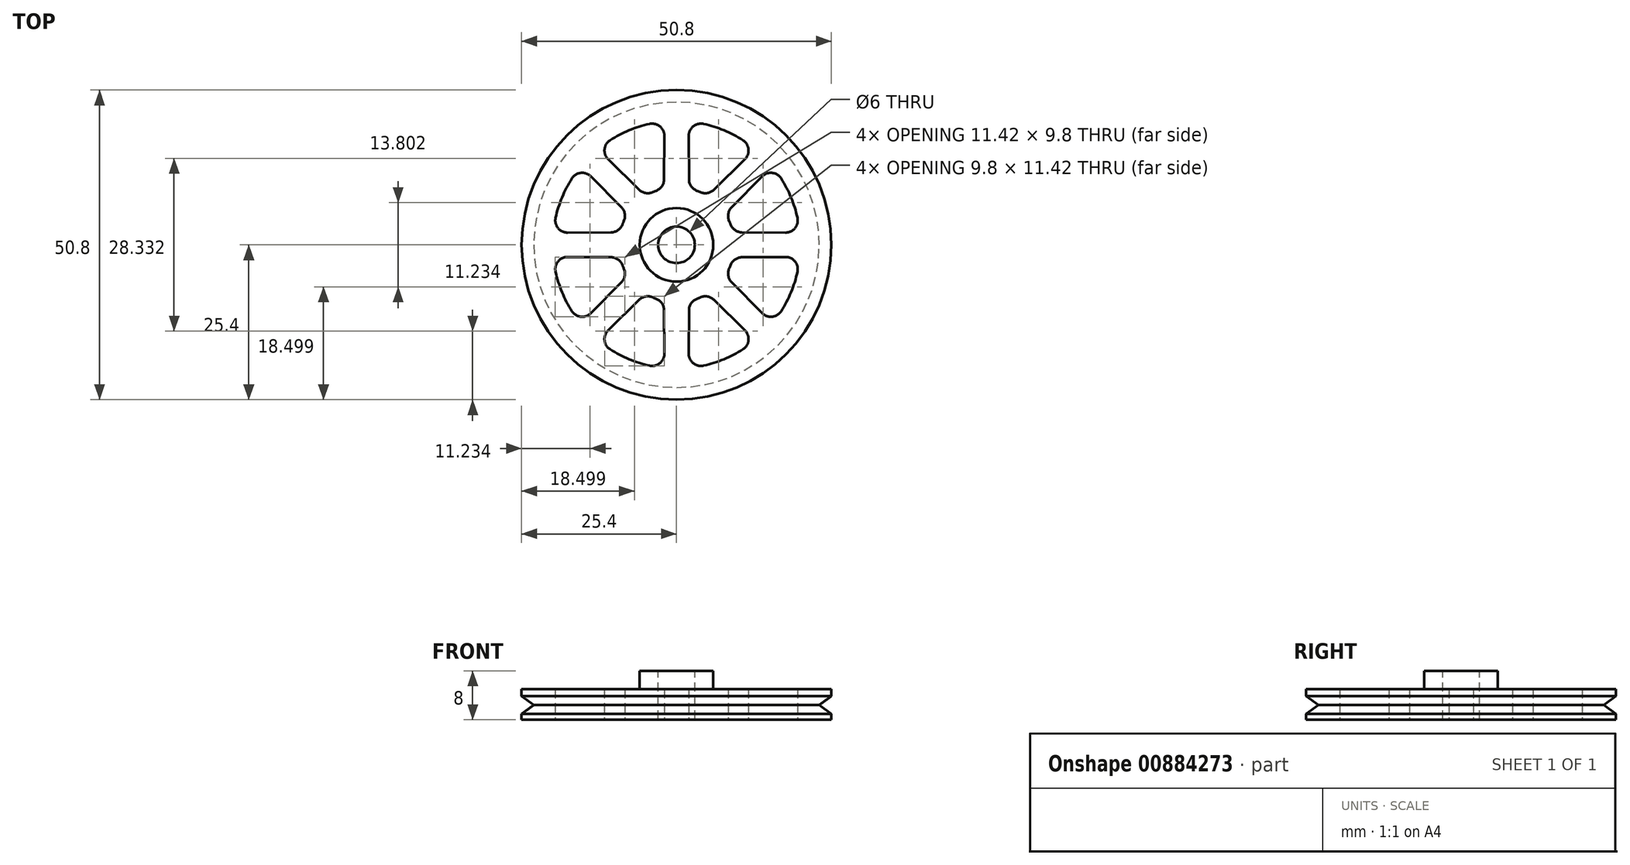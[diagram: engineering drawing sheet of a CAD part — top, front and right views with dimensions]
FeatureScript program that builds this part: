
annotation { "Feature Type Name" : "Feature", "Feature Type Description" : "" }
export const myFeature = defineFeature(function(context is Context, id is Id, definition is map)
    precondition{}
    {
        {
            var Q0;
            Q0=qCreatedBy(makeId("Top.planeOp"),FACE);
            var sketch = newSketch(context, id + "F0", { "sketchPlane" : qUnion([Q0])});
            skCircle(sketch, "E0", {"center": v(0, 0) * mm, "radius": 25.4 * mm});
            skCircle(sketch, "E1", {"center": v(0, 0) * mm, "radius": 3.12 * mm});
            skArc(sketch, "E2.0", {"start": v(-4.44, 19.83) * mm, "mid": v(-7.78, 18.77) * mm, "end": v(-10.88, 17.16) * mm});
            skArc(sketch, "E3.0", {"start": v(-3.34, 8.87) * mm, "mid": v(-3.63, 8.75) * mm, "end": v(-3.9, 8.63) * mm});
            skLineSegment(sketch, "E4.0", {"start": v(-2, 17.87) * mm, "end": v(-2.04, 10.73) * mm});
            skLineSegment(sketch, "E5.0", {"start": v(2, 17.87) * mm, "end": v(2.04, 10.73) * mm});
            skPoint(sketch, "E6.orphan", {"position": v(0, 22.85) * mm});
            skPoint(sketch, "E7.visualSharp", {"position": v(-1.99, 20.22) * mm});
            skArc(sketch, "E7.filletArc", {"start": v(-2, 17.87) * mm, "mid": v(-2.74, 19.44) * mm, "end": v(-4.44, 19.83) * mm});
            skPoint(sketch, "E8.visualSharp", {"position": v(1.99, 20.22) * mm});
            skArc(sketch, "E8.filletArc", {"start": v(4.44, 19.83) * mm, "mid": v(2.74, 19.44) * mm, "end": v(2, 17.87) * mm});
            skPoint(sketch, "E9.visualSharp", {"position": v(-2.05, 9.25) * mm});
            skArc(sketch, "E9.filletArc", {"start": v(-3.34, 8.87) * mm, "mid": v(-2.4, 9.6) * mm, "end": v(-2.04, 10.73) * mm});
            skPoint(sketch, "E10.visualSharp", {"position": v(2.05, 9.25) * mm});
            skArc(sketch, "E10.filletArc", {"start": v(2.04, 10.73) * mm, "mid": v(2.4, 9.6) * mm, "end": v(3.34, 8.87) * mm});
            skArc(sketch, "E11.1.0", {"start": v(-14.05, 11.22) * mm, "mid": v(-15.68, 11.8) * mm, "end": v(-17.16, 10.88) * mm});
            skLineSegment(sketch, "E11.1.1", {"start": v(-14.05, 11.22) * mm, "end": v(-9.03, 6.14) * mm});
            skArc(sketch, "E11.1.2", {"start": v(-8.63, 3.9) * mm, "mid": v(-8.48, 5.09) * mm, "end": v(-9.03, 6.14) * mm});
            skArc(sketch, "E11.1.3", {"start": v(-10.88, 17.16) * mm, "mid": v(-11.8, 15.68) * mm, "end": v(-11.22, 14.05) * mm});
            skLineSegment(sketch, "E11.1.4", {"start": v(-11.22, 14.05) * mm, "end": v(-6.14, 9.03) * mm});
            skArc(sketch, "E11.1.5", {"start": v(-6.14, 9.03) * mm, "mid": v(-5.09, 8.48) * mm, "end": v(-3.9, 8.63) * mm});
            skArc(sketch, "E11.2.0", {"start": v(-17.87, -2) * mm, "mid": v(-19.44, -2.74) * mm, "end": v(-19.83, -4.44) * mm});
            skLineSegment(sketch, "E11.2.1", {"start": v(-17.87, -2) * mm, "end": v(-10.73, -2.04) * mm});
            skArc(sketch, "E11.2.2", {"start": v(-8.87, -3.34) * mm, "mid": v(-9.6, -2.4) * mm, "end": v(-10.73, -2.04) * mm});
            skArc(sketch, "E11.2.3", {"start": v(-19.83, 4.44) * mm, "mid": v(-19.44, 2.74) * mm, "end": v(-17.87, 2) * mm});
            skLineSegment(sketch, "E11.2.4", {"start": v(-17.87, 2) * mm, "end": v(-10.73, 2.04) * mm});
            skArc(sketch, "E11.2.5", {"start": v(-10.73, 2.04) * mm, "mid": v(-9.6, 2.4) * mm, "end": v(-8.87, 3.34) * mm});
            skArc(sketch, "E11.3.0", {"start": v(-11.22, -14.05) * mm, "mid": v(-11.8, -15.68) * mm, "end": v(-10.88, -17.16) * mm});
            skLineSegment(sketch, "E11.3.1", {"start": v(-11.22, -14.05) * mm, "end": v(-6.14, -9.03) * mm});
            skArc(sketch, "E11.3.2", {"start": v(-3.9, -8.63) * mm, "mid": v(-5.09, -8.48) * mm, "end": v(-6.14, -9.03) * mm});
            skArc(sketch, "E11.3.3", {"start": v(-17.16, -10.88) * mm, "mid": v(-15.68, -11.8) * mm, "end": v(-14.05, -11.22) * mm});
            skLineSegment(sketch, "E11.3.4", {"start": v(-14.05, -11.22) * mm, "end": v(-9.03, -6.14) * mm});
            skArc(sketch, "E11.3.5", {"start": v(-9.03, -6.14) * mm, "mid": v(-8.48, -5.09) * mm, "end": v(-8.63, -3.9) * mm});
            skArc(sketch, "E11.4.0", {"start": v(2, -17.87) * mm, "mid": v(2.74, -19.44) * mm, "end": v(4.44, -19.83) * mm});
            skLineSegment(sketch, "E11.4.1", {"start": v(2, -17.87) * mm, "end": v(2.04, -10.73) * mm});
            skArc(sketch, "E11.4.2", {"start": v(3.34, -8.87) * mm, "mid": v(2.4, -9.6) * mm, "end": v(2.04, -10.73) * mm});
            skArc(sketch, "E11.4.3", {"start": v(-4.44, -19.83) * mm, "mid": v(-2.74, -19.44) * mm, "end": v(-2, -17.87) * mm});
            skLineSegment(sketch, "E11.4.4", {"start": v(-2, -17.87) * mm, "end": v(-2.04, -10.73) * mm});
            skArc(sketch, "E11.4.5", {"start": v(-2.04, -10.73) * mm, "mid": v(-2.4, -9.6) * mm, "end": v(-3.34, -8.87) * mm});
            skArc(sketch, "E11.5.0", {"start": v(14.05, -11.22) * mm, "mid": v(15.68, -11.8) * mm, "end": v(17.16, -10.88) * mm});
            skLineSegment(sketch, "E11.5.1", {"start": v(14.05, -11.22) * mm, "end": v(9.03, -6.14) * mm});
            skArc(sketch, "E11.5.2", {"start": v(8.63, -3.9) * mm, "mid": v(8.48, -5.09) * mm, "end": v(9.03, -6.14) * mm});
            skArc(sketch, "E11.5.3", {"start": v(10.88, -17.16) * mm, "mid": v(11.8, -15.68) * mm, "end": v(11.22, -14.05) * mm});
            skLineSegment(sketch, "E11.5.4", {"start": v(11.22, -14.05) * mm, "end": v(6.14, -9.03) * mm});
            skArc(sketch, "E11.5.5", {"start": v(6.14, -9.03) * mm, "mid": v(5.09, -8.48) * mm, "end": v(3.9, -8.63) * mm});
            skArc(sketch, "E11.6.0", {"start": v(17.87, 2) * mm, "mid": v(19.44, 2.74) * mm, "end": v(19.83, 4.44) * mm});
            skLineSegment(sketch, "E11.6.1", {"start": v(17.87, 2) * mm, "end": v(10.73, 2.04) * mm});
            skArc(sketch, "E11.6.2", {"start": v(8.87, 3.34) * mm, "mid": v(9.6, 2.4) * mm, "end": v(10.73, 2.04) * mm});
            skArc(sketch, "E11.6.3", {"start": v(19.83, -4.44) * mm, "mid": v(19.44, -2.74) * mm, "end": v(17.87, -2) * mm});
            skLineSegment(sketch, "E11.6.4", {"start": v(17.87, -2) * mm, "end": v(10.73, -2.04) * mm});
            skArc(sketch, "E11.6.5", {"start": v(10.73, -2.04) * mm, "mid": v(9.6, -2.4) * mm, "end": v(8.87, -3.34) * mm});
            skArc(sketch, "E11.7.0", {"start": v(11.22, 14.05) * mm, "mid": v(11.8, 15.68) * mm, "end": v(10.88, 17.16) * mm});
            skLineSegment(sketch, "E11.7.1", {"start": v(11.22, 14.05) * mm, "end": v(6.14, 9.03) * mm});
            skArc(sketch, "E11.7.2", {"start": v(3.9, 8.63) * mm, "mid": v(5.09, 8.48) * mm, "end": v(6.14, 9.03) * mm});
            skArc(sketch, "E11.7.3", {"start": v(17.16, 10.88) * mm, "mid": v(15.68, 11.8) * mm, "end": v(14.05, 11.22) * mm});
            skLineSegment(sketch, "E11.7.4", {"start": v(14.05, 11.22) * mm, "end": v(9.03, 6.14) * mm});
            skArc(sketch, "E11.7.5", {"start": v(9.03, 6.14) * mm, "mid": v(8.48, 5.09) * mm, "end": v(8.63, 3.9) * mm});
            skArc(sketch, "E12.trimOffspring", {"start": v(-17.16, 10.88) * mm, "mid": v(-18.77, 7.78) * mm, "end": v(-19.83, 4.44) * mm});
            skArc(sketch, "E13.trimOffspring", {"start": v(-8.63, 3.9) * mm, "mid": v(-8.75, 3.63) * mm, "end": v(-8.87, 3.34) * mm});
            skArc(sketch, "E14.trimOffspring", {"start": v(-8.87, -3.34) * mm, "mid": v(-8.75, -3.63) * mm, "end": v(-8.63, -3.9) * mm});
            skArc(sketch, "E15.trimOffspring", {"start": v(-19.83, -4.44) * mm, "mid": v(-18.77, -7.78) * mm, "end": v(-17.16, -10.88) * mm});
            skArc(sketch, "E16.trimOffspring", {"start": v(-10.88, -17.16) * mm, "mid": v(-7.78, -18.77) * mm, "end": v(-4.44, -19.83) * mm});
            skArc(sketch, "E17.trimOffspring", {"start": v(-3.9, -8.63) * mm, "mid": v(-3.63, -8.75) * mm, "end": v(-3.34, -8.87) * mm});
            skArc(sketch, "E18.trimOffspring", {"start": v(3.34, -8.87) * mm, "mid": v(3.63, -8.75) * mm, "end": v(3.9, -8.63) * mm});
            skArc(sketch, "E19.trimOffspring", {"start": v(8.63, -3.9) * mm, "mid": v(8.75, -3.63) * mm, "end": v(8.87, -3.34) * mm});
            skArc(sketch, "E20.trimOffspring", {"start": v(8.87, 3.34) * mm, "mid": v(8.75, 3.63) * mm, "end": v(8.63, 3.9) * mm});
            skArc(sketch, "E21.trimOffspring", {"start": v(3.9, 8.63) * mm, "mid": v(3.63, 8.75) * mm, "end": v(3.34, 8.87) * mm});
            skArc(sketch, "E22.trimOffspring", {"start": v(10.88, 17.16) * mm, "mid": v(7.78, 18.77) * mm, "end": v(4.44, 19.83) * mm});
            skArc(sketch, "E23.trimOffspring", {"start": v(19.83, 4.44) * mm, "mid": v(18.77, 7.78) * mm, "end": v(17.16, 10.88) * mm});
            skArc(sketch, "E24.trimOffspring", {"start": v(17.16, -10.88) * mm, "mid": v(18.77, -7.78) * mm, "end": v(19.83, -4.44) * mm});
            skArc(sketch, "E25.trimOffspring", {"start": v(4.44, -19.83) * mm, "mid": v(7.78, -18.77) * mm, "end": v(10.88, -17.16) * mm});
            skSolve(sketch);
        }
        {
            var Q0;
            Q0=makeQuery(id+"F0.imprint","IMPRINT",FACE,{"disambiguationData":[TD([[makeQuery(id+"F0.imprint","IMPRINT",EDGE,{"derivedFrom":sQuery(id+"F0.wireOp",EDGE,"E0")}),1.0]])]});
            extrude(context, id + "F1", {"entities" : qUnion([Q0]), "depth" : 5 * mm, "offsetDistance" : 25.4 * mm});
        }
        {
            var Q0;
            Q0=qCreatedBy(makeId("Top.planeOp"),FACE);
            var sketch = newSketch(context, id + "F2", { "sketchPlane" : qUnion([Q0])});
            skCircle(sketch, "E26", {"center": v(0, 0) * mm, "radius": 6.03 * mm});
            skSolve(sketch);
        }
        {
            var Q0;
            Q0=makeQuery(id+"F2.imprint","IMPRINT",FACE,{"disambiguationData":[TD([[makeQuery(id+"F2.imprint","IMPRINT",EDGE,{"derivedFrom":sQuery(id+"F2.wireOp",EDGE,"E26")}),1.0]])]});
            extrude(context, id + "F3", {"entities" : qUnion([Q0]), "operationType" : NewBodyOperationType.ADD, "depth" : 8 * mm, "offsetDistance" : 25.4 * mm});
        }
        {
            var Q0;
            Q0=makeQuery(id+"F3.opExtrude","CAP_FACE",FACE,{"disambiguationData":[OSD([sQuery(id+"F2.wireOp",EDGE,"E26")])],"isStart":false});
            var sketch = newSketch(context, id + "F4", { "sketchPlane" : qUnion([Q0])});
            skCircle(sketch, "E27", {"center": v(0, 0) * mm, "radius": 3 * mm});
            skSolve(sketch);
        }
        {
            var Q0;
            Q0=makeQuery(id+"F4.imprint","IMPRINT",FACE,{"disambiguationData":[TD([[makeQuery(id+"F4.imprint","IMPRINT",EDGE,{"derivedFrom":sQuery(id+"F4.wireOp",EDGE,"E27")}),1.0]])]});
            extrude(context, id + "F5", {"entities" : qUnion([Q0]), "operationType" : NewBodyOperationType.REMOVE, "endBound" : BoundingType.THROUGH_ALL, "oppositeDirection" : true, "depth" : 25.4 * mm, "offsetDistance" : 25.4 * mm});
        }
        {
            var Q0;
            Q0=qCreatedBy(makeId("Right.planeOp"),FACE);
            var sketch = newSketch(context, id + "F6", { "sketchPlane" : qUnion([Q0])});
            skLineSegment(sketch, "E28", {"start": v(25.4, 2.4) * mm, "end": v(23.4, 2.4) * mm});
            skLineSegment(sketch, "E29", {"start": v(23.4, 2.4) * mm, "end": v(25.46, 3.9) * mm});
            skLineSegment(sketch, "E30", {"start": v(25.46, 3.9) * mm, "end": v(25.4, 2.4) * mm});
            skLineSegment(sketch, "E31.MirrorCS", {"start": v(23.4, 2.4) * mm, "end": v(25.46, 0.9) * mm});
            skLineSegment(sketch, "E32.MirrorCS", {"start": v(25.46, 0.9) * mm, "end": v(25.4, 2.4) * mm});
            skLineSegment(sketch, "E33", {"start": v(0, 19.4) * mm, "end": v(0, -3.2) * mm, "construction": true});
            skSolve(sketch);
        }
        {
            var Q0;
            Q0 = qSketchRegion(id + "F6", true);
            var Q1;
            Q1=sQuery(id+"F6.wireOp",EDGE,"E33");
            revolve(context, id + "F7", {"operationType" : NewBodyOperationType.REMOVE, "surfaceOperationType" : NewSurfaceOperationType.NEW, "entities" : qUnion([Q0]), "axis" : qUnion([Q1]), "revolveType" : RevolveType.FULL, "oppositeDirection" : true});
        }
    });
